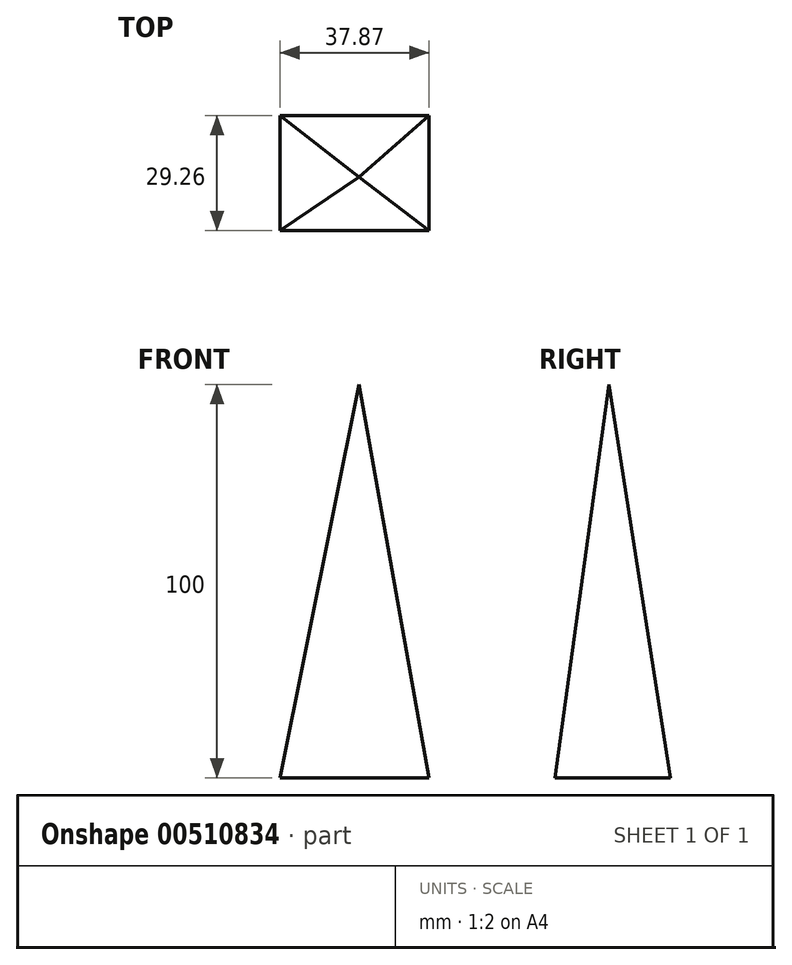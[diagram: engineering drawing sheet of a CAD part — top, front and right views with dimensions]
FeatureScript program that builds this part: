
annotation { "Feature Type Name" : "Feature", "Feature Type Description" : "" }
export const myFeature = defineFeature(function(context is Context, id is Id, definition is map)
    precondition{}
    {
        {
            var Q0;
            Q0=qCreatedBy(makeId("Top.planeOp"),FACE);
            var sketch = newSketch(context, id + "F0", { "sketchPlane" : qUnion([Q0])});
            skLineSegment(sketch, "E0.bottom", {"start": v(-22.1, -5.88) * mm, "end": v(15.78, -5.88) * mm});
            skLineSegment(sketch, "E0.top", {"start": v(-22.1, 23.38) * mm, "end": v(15.78, 23.38) * mm});
            skLineSegment(sketch, "E0.left", {"start": v(-22.1, -5.88) * mm, "end": v(-22.1, 23.38) * mm});
            skLineSegment(sketch, "E0.right", {"start": v(15.78, -5.88) * mm, "end": v(15.78, 23.38) * mm});
            skPoint(sketch, "E0.middle", {"position": v(-3.16, 8.75) * mm});
            skSolve(sketch);
        }
        {
            var Q0;
            Q0=qCreatedBy(makeId("Top.planeOp"),FACE);
            cPlane(context, id + "F1", {"entities" : qUnion([Q0]), "cplaneType" : CPlaneType.OFFSET, "offset" : 100 * mm, "width" : 150 * mm, "height" : 150 * mm});
        }
        {
            var Q0;
            Q0=qCreatedBy(id+"F1.planeOp",FACE);
            var sketch = newSketch(context, id + "F2", { "sketchPlane" : qUnion([Q0])});
            skPoint(sketch, "E1", {"position": v(-1.98, 7.8) * mm});
            skSolve(sketch);
        }
        {
            var Q0;
            Q0=makeQuery(id+"F0.imprint","IMPRINT",FACE,{"disambiguationData":[TD([[makeQuery(id+"F0.imprint","IMPRINT",EDGE,{"derivedFrom":sQuery(id+"F0.wireOp",EDGE,"E0.bottom")}),1.0]])]});
            var Q1;
            Q1=sQuery(id+"F2.wireOp",VERTEX,"E1");
            loft(context, id + "F3", {"sheetProfilesArray" : [{ "sheetProfileEntities" : qUnion([Q0]) }, { "sheetProfileEntities" : qUnion([Q1]) }]});
        }
    });
